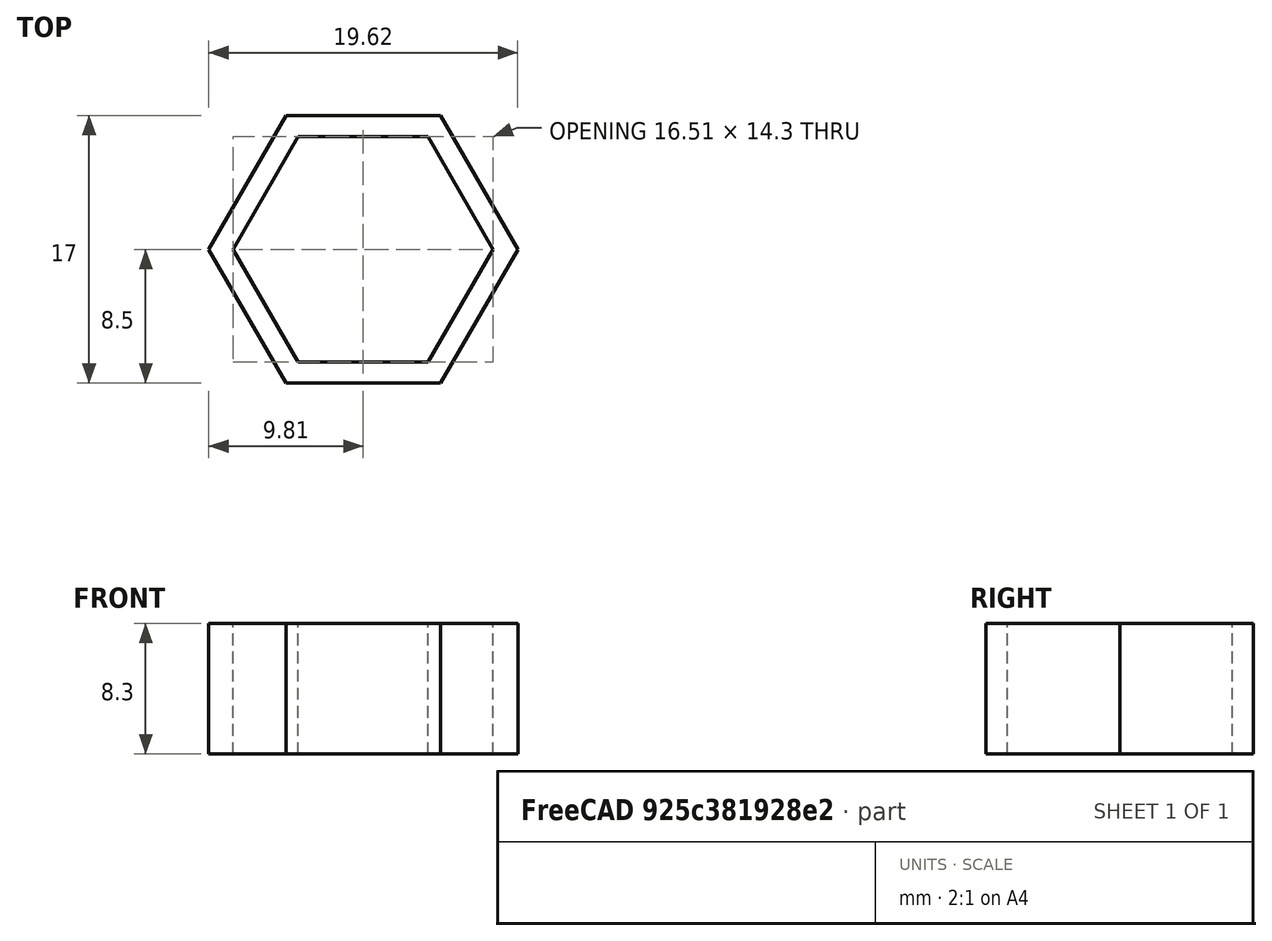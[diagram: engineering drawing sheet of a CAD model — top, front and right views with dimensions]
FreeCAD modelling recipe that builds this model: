
FCSTD DOCUMENT  (FreeCAD 0.21R33771 (Git))
Label: luva-hexagonal
License: All rights reserved
LicenseURL: https://en.wikipedia.org/wiki/All_rights_reserved
objects: Sketcher::SketchObject×1, PartDesign::Pad×1, PartDesign::Body×1
note: 4 computed .brp shape members not serialized (recipe doc carries the construction recipe); baked Part::Feature solids carry a one-line shape summary decoded from their .brp

FEATURE [Sketcher::SketchObject] Sketch
  FullyConstrained = true
  MapMode = 5
  Support = -> [XY_Plane]
  sketch-geometry (14):
    g0: LineSegment StartX=-4.12805 StartY=-7.15 StartZ=0 EndX=4.12805 EndY=-7.15 EndZ=0
    g1: LineSegment StartX=4.12805 StartY=-7.15 StartZ=0 EndX=8.25611 EndY=0 EndZ=0
    g2: LineSegment StartX=8.25611 StartY=0 StartZ=0 EndX=4.12805 EndY=7.15 EndZ=0
    g3: LineSegment StartX=4.12805 StartY=7.15 StartZ=0 EndX=-4.12805 EndY=7.15 EndZ=0
    g4: LineSegment StartX=-4.12805 StartY=7.15 StartZ=0 EndX=-8.25611 EndY=-1.8e-15 EndZ=0
    g5: LineSegment StartX=-8.25611 StartY=-1.6e-15 StartZ=0 EndX=-4.12805 EndY=-7.15 EndZ=0
    g6: Circle CenterX=0 CenterY=0 CenterZ=0 NormalX=0 NormalY=0 NormalZ=1 AngleXU=0 Radius=8.25611
    g7: LineSegment StartX=-4.90748 StartY=8.5 StartZ=0 EndX=-9.81495 EndY=0 EndZ=0
    g8: LineSegment StartX=-9.81495 StartY=0 StartZ=0 EndX=-4.90748 EndY=-8.5 EndZ=0
    g9: LineSegment StartX=-4.90748 StartY=-8.5 StartZ=0 EndX=4.90748 EndY=-8.5 EndZ=0
    g10: LineSegment StartX=4.90748 StartY=-8.5 StartZ=0 EndX=9.81495 EndY=0 EndZ=0
    g11: LineSegment StartX=9.81495 StartY=0 StartZ=0 EndX=4.90748 EndY=8.5 EndZ=0
    g12: LineSegment StartX=4.90748 StartY=8.5 StartZ=0 EndX=-4.90748 EndY=8.5 EndZ=0
    g13: Circle CenterX=0 CenterY=0 CenterZ=0 NormalX=0 NormalY=0 NormalZ=1 AngleXU=0 Radius=9.81495
  constraints (32):
    c: Coincident(g0,g1)
    c: Coincident(g1,g2)
    c: Coincident(g2,g3)
    c: Coincident(g3,g4)
    c: Coincident(g4,g5)
    c: Coincident(g5,g0)
    c: Equal(g0, g1-g5) x5
    c: PointOnObject(g0,g6)
    c: PointOnObject(g1,g6)
    c: PointOnObject(g2,g6)
    c: PointOnObject(g3,g6)
    c: PointOnObject(g4,g6)
    c: PointOnObject(g5,g6)
    c: Coincident(g6,g-1)
    c: Horizontal(g3)
    c: DistanceY(g0,g2) = 14.3
    c: Coincident(g7,g8)
    c: Coincident(g8,g9)
    c: Coincident(g9,g10)
    c: Coincident(g10,g11)
    c: Coincident(g11,g12)
    c: Coincident(g12,g7)
    c: Equal(g7, g8-g12) x5
    c: PointOnObject(g7,g13)
    c: PointOnObject(g8,g13)
    c: PointOnObject(g9,g13)
    c: PointOnObject(g10,g13)
    c: PointOnObject(g11,g13)
    c: PointOnObject(g12,g13)
    c: Coincident(g13,g6)
    c: Horizontal(g12)
    c: DistanceY(g9,g11) = 17
FEATURE [PartDesign::Pad] Pad
  Direction = (0,0,1)
  Length = 8.3
  Length2 = 10
  Profile = -> Sketch
  ReferenceAxis = -> Sketch [N_Axis]
  Type = 0
FEATURE [PartDesign::Body] Body
  Group = -> [Sketch,Pad]
  Origin = -> Origin
  Tip = -> Pad
